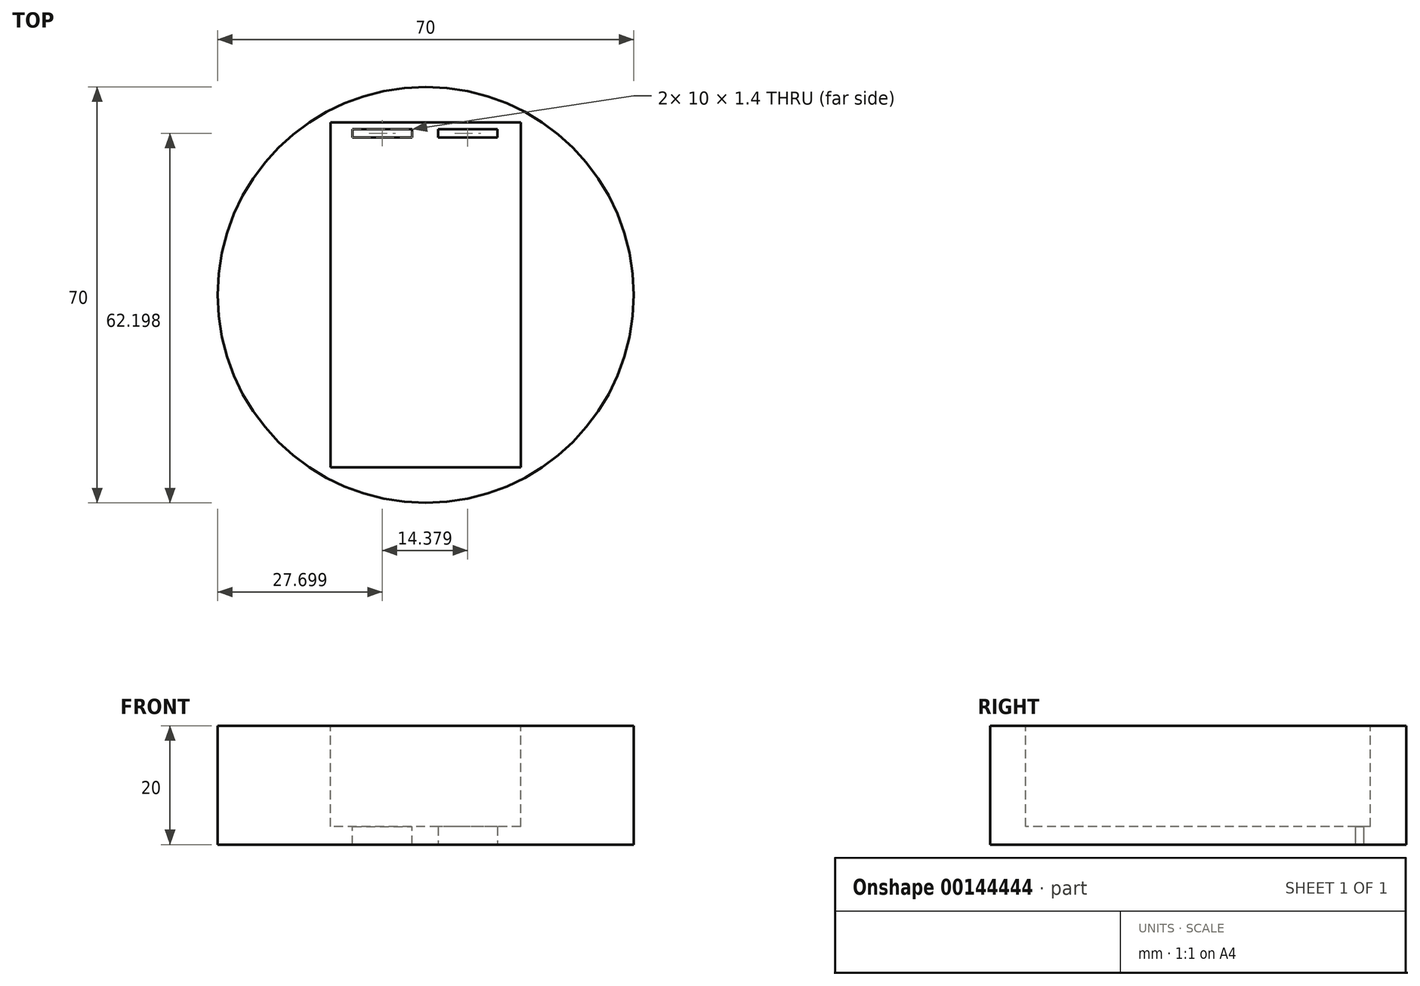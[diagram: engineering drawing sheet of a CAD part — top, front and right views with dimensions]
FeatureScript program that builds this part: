
annotation { "Feature Type Name" : "Feature", "Feature Type Description" : "" }
export const myFeature = defineFeature(function(context is Context, id is Id, definition is map)
    precondition{}
    {
        {
            var Q0;
            Q0=qCreatedBy(makeId("Top.planeOp"),FACE);
            var sketch = newSketch(context, id + "F0", { "sketchPlane" : qUnion([Q0])});
            skCircle(sketch, "E0", {"center": v(0, 0) * mm, "radius": 35 * mm});
            skSolve(sketch);
        }
        {
            var Q0;
            Q0=makeQuery(id+"F0.imprint","IMPRINT",FACE,{"disambiguationData":[TD([[makeQuery(id+"F0.imprint","IMPRINT",EDGE,{"derivedFrom":sQuery(id+"F0.wireOp",EDGE,"E0")}),1.0]])]});
            var Q1;
            Q1=sQuery(id+"F0.wireOp",EDGE,"E0");
            extrude(context, id + "F1", {"entities" : qUnion([Q0]), "surfaceEntities" : qUnion([Q1]), "depth" : 20 * mm});
        }
        {
            var Q0;
            Q0=makeQuery(id+"F1.opExtrude","CAP_FACE",FACE,{"disambiguationData":[OSD([sQuery(id+"F0.wireOp",EDGE,"E0")])],"isStart":false});
            var sketch = newSketch(context, id + "F2", { "sketchPlane" : qUnion([Q0])});
            skLineSegment(sketch, "E1.bottom", {"start": v(16, 29) * mm, "end": v(-16, 29) * mm});
            skLineSegment(sketch, "E1.top", {"start": v(16, -29) * mm, "end": v(-16, -29) * mm});
            skLineSegment(sketch, "E1.left", {"start": v(16, 29) * mm, "end": v(16, -29) * mm});
            skLineSegment(sketch, "E1.right", {"start": v(-16, 29) * mm, "end": v(-16, -29) * mm});
            skPoint(sketch, "E1.middle", {"position": v(0, 0) * mm});
            skSolve(sketch);
        }
        {
            var Q0;
            Q0 = qSketchRegion(id + "F2", true);
            extrude(context, id + "F3", {"entities" : qUnion([Q0]), "operationType" : NewBodyOperationType.REMOVE, "oppositeDirection" : true, "depth" : 17 * mm});
        }
        {
            var Q0;
            Q0=makeQuery(id+"F3.boolean.opBoolean","COPY",FACE,{"derivedFrom":makeQuery(id+"F3.opExtrude","CAP_FACE",FACE,{"disambiguationData":[OSD([sQuery(id+"F2.wireOp",EDGE,"E1.bottom"),sQuery(id+"F2.wireOp",EDGE,"E1.top"),sQuery(id+"F2.wireOp",EDGE,"E1.left"),sQuery(id+"F2.wireOp",EDGE,"E1.right")])],"isStart":false})});
            var sketch = newSketch(context, id + "F4", { "sketchPlane" : qUnion([Q0])});
            skLineSegment(sketch, "E2.bottom", {"start": v(-12.3, 27.9) * mm, "end": v(-2.3, 27.9) * mm});
            skLineSegment(sketch, "E2.top", {"start": v(-12.3, 26.5) * mm, "end": v(-2.3, 26.5) * mm});
            skLineSegment(sketch, "E2.left", {"start": v(-12.3, 27.9) * mm, "end": v(-12.3, 26.5) * mm});
            skLineSegment(sketch, "E2.right", {"start": v(-2.3, 27.9) * mm, "end": v(-2.3, 26.5) * mm});
            skSolve(sketch);
        }
        {
            var Q0;
            Q0 = qSketchRegion(id + "F4", true);
            extrude(context, id + "F5", {"entities" : qUnion([Q0]), "operationType" : NewBodyOperationType.REMOVE, "oppositeDirection" : true, "depth" : 5 * mm});
        }
        {
            var Q0;
            Q0=qCreatedBy(makeId("Top.planeOp"),FACE);
            var sketch = newSketch(context, id + "F6", { "sketchPlane" : qUnion([Q0])});
            skLineSegment(sketch, "E3.bottom", {"start": v(2.08, 27.86) * mm, "end": v(12.08, 27.86) * mm});
            skLineSegment(sketch, "E3.top", {"start": v(2.08, 26.46) * mm, "end": v(12.08, 26.46) * mm});
            skLineSegment(sketch, "E3.left", {"start": v(2.08, 27.86) * mm, "end": v(2.08, 26.46) * mm});
            skLineSegment(sketch, "E3.right", {"start": v(12.08, 27.86) * mm, "end": v(12.08, 26.46) * mm});
            skSolve(sketch);
        }
        {
            var Q0;
            Q0 = qSketchRegion(id + "F6", true);
            extrude(context, id + "F7", {"entities" : qUnion([Q0]), "operationType" : NewBodyOperationType.REMOVE, "depth" : 5 * mm});
        }
    });
